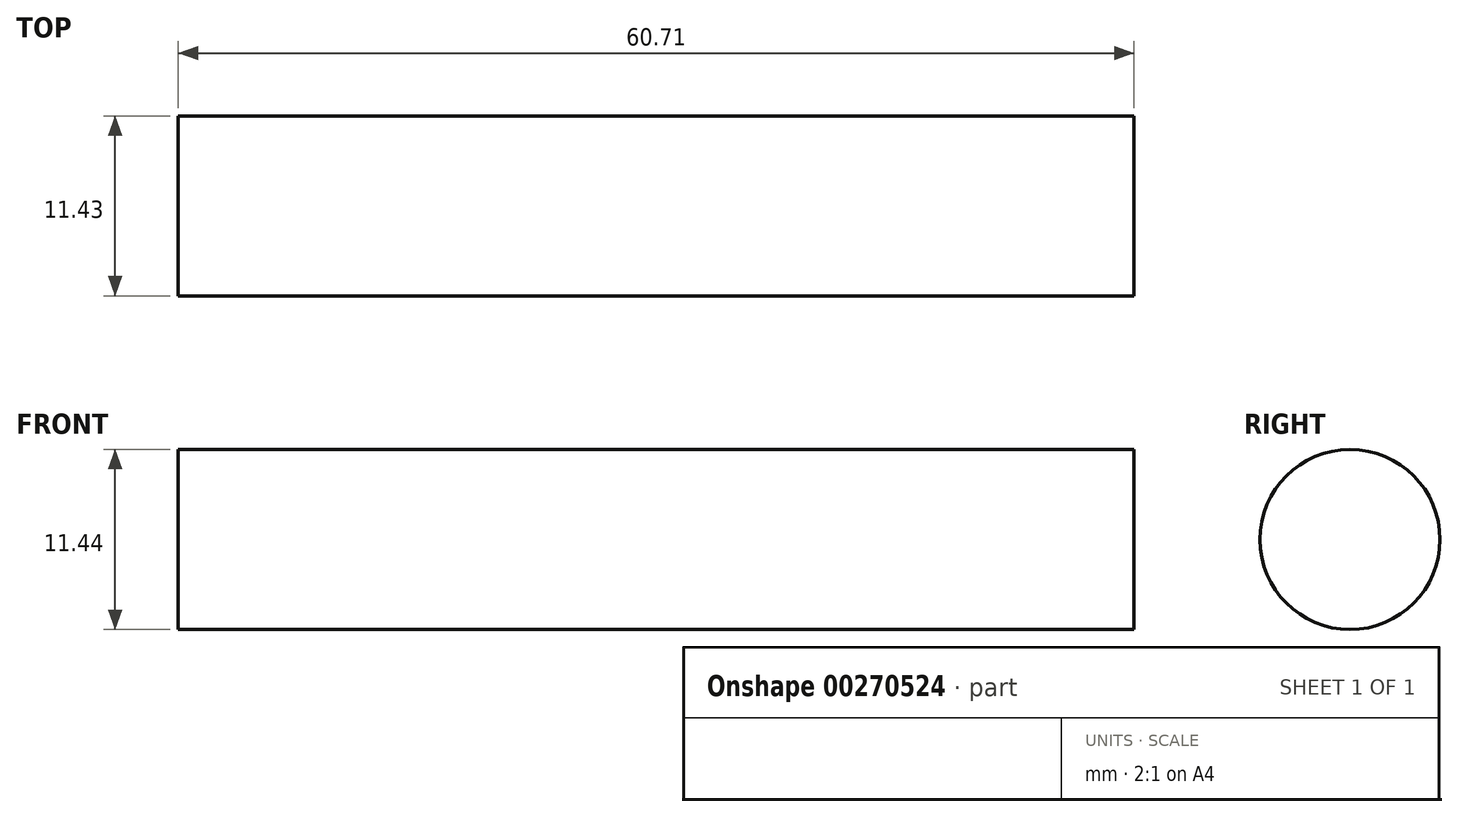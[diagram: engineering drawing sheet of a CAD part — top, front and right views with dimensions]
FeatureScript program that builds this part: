
annotation { "Feature Type Name" : "Feature", "Feature Type Description" : "" }
export const myFeature = defineFeature(function(context is Context, id is Id, definition is map)
    precondition{}
    {
        {
            var Q0;
            Q0=qCreatedBy(makeId("Right.planeOp"),FACE);
            var sketch = newSketch(context, id + "F0", { "sketchPlane" : qUnion([Q0])});
            skCircle(sketch, "E0", {"center": v(-57.07, 42.8) * mm, "radius": 5.72 * mm});
            skSolve(sketch);
        }
        {
            var Q0;
            Q0=makeQuery(id+"F0.imprint","IMPRINT",FACE,{"disambiguationData":[TD([[makeQuery(id+"F0.imprint","IMPRINT",EDGE,{"derivedFrom":sQuery(id+"F0.wireOp",EDGE,"E0")}),1.0]])]});
            extrude(context, id + "F1", {"entities" : qUnion([Q0]), "depth" : 60.7 * mm});
        }
    });
